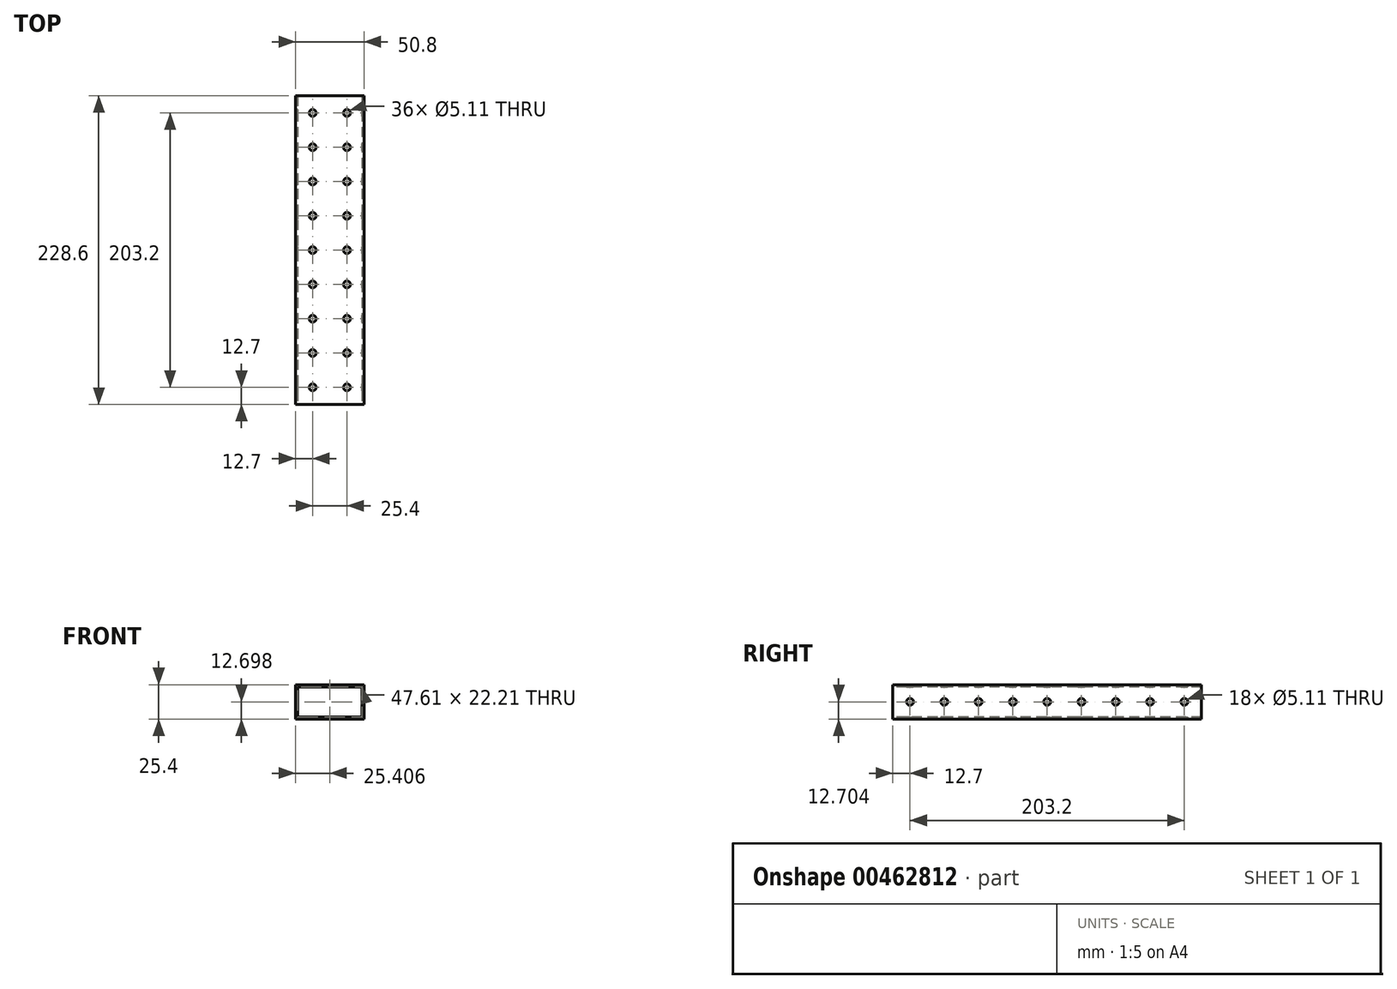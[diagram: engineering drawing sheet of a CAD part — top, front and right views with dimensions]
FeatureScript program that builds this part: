
annotation { "Feature Type Name" : "Feature", "Feature Type Description" : "" }
export const myFeature = defineFeature(function(context is Context, id is Id, definition is map)
    precondition{}
    {
        {
            var Q0;
            Q0=qCreatedBy(makeId("Front.planeOp"),FACE);
            var sketch = newSketch(context, id + "F0", { "sketchPlane" : qUnion([Q0])});
            skLineSegment(sketch, "E0.bottom", {"start": v(-25.4, -41.59) * mm, "end": v(25.4, -41.59) * mm});
            skLineSegment(sketch, "E0.top", {"start": v(-25.4, -66.99) * mm, "end": v(25.4, -66.99) * mm});
            skLineSegment(sketch, "E0.left", {"start": v(-25.4, -41.59) * mm, "end": v(-25.4, -66.99) * mm});
            skLineSegment(sketch, "E0.right", {"start": v(25.4, -41.59) * mm, "end": v(25.4, -66.99) * mm});
            skSolve(sketch);
        }
        {
            var Q0;
            Q0=makeQuery(id+"F0.imprint","IMPRINT",FACE,{"disambiguationData":[TD([[makeQuery(id+"F0.imprint","IMPRINT",EDGE,{"derivedFrom":sQuery(id+"F0.wireOp",EDGE,"E0.bottom")}),-1.0]])]});
            extrude(context, id + "F1", {"entities" : qUnion([Q0]), "depth" : 228.6 * mm});
        }
        {
            var Q0;
            Q0=makeQuery(id+"F1.opExtrude","SWEPT_FACE",FACE,{"disambiguationData":[OSD([sQuery(id+"F0.wireOp",EDGE,"E0.top")])]});
            var sketch = newSketch(context, id + "F2", { "sketchPlane" : qUnion([Q0])});
            skCircle(sketch, "E1", {"center": v(-12.7, 215.9) * mm, "radius": 2.55 * mm});
            skCircle(sketch, "E2.0.1.0", {"center": v(-12.7, 190.5) * mm, "radius": 2.55 * mm});
            skCircle(sketch, "E2.0.2.0", {"center": v(-12.7, 165.1) * mm, "radius": 2.55 * mm});
            skCircle(sketch, "E2.0.3.0", {"center": v(-12.7, 139.7) * mm, "radius": 2.55 * mm});
            skCircle(sketch, "E2.0.4.0", {"center": v(-12.7, 114.3) * mm, "radius": 2.55 * mm});
            skCircle(sketch, "E2.0.5.0", {"center": v(-12.7, 88.9) * mm, "radius": 2.55 * mm});
            skCircle(sketch, "E2.1.0.0", {"center": v(12.7, 215.9) * mm, "radius": 2.55 * mm});
            skCircle(sketch, "E2.1.1.0", {"center": v(12.7, 190.5) * mm, "radius": 2.55 * mm});
            skCircle(sketch, "E2.1.2.0", {"center": v(12.7, 165.1) * mm, "radius": 2.55 * mm});
            skCircle(sketch, "E2.1.3.0", {"center": v(12.7, 139.7) * mm, "radius": 2.55 * mm});
            skCircle(sketch, "E2.1.4.0", {"center": v(12.7, 114.3) * mm, "radius": 2.55 * mm});
            skCircle(sketch, "E2.1.5.0", {"center": v(12.7, 88.9) * mm, "radius": 2.55 * mm});
            skLineSegment(sketch, "E2.direction1", {"start": v(-12.7, 215.9) * mm, "end": v(12.7, 215.9) * mm, "construction": true});
            skLineSegment(sketch, "E2.direction2", {"start": v(-12.7, 215.9) * mm, "end": v(-12.7, 190.5) * mm, "construction": true});
            skCircle(sketch, "E3.0.0.6", {"center": v(-12.7, 63.5) * mm, "radius": 2.55 * mm});
            skCircle(sketch, "E3.0.1.6", {"center": v(12.7, 63.5) * mm, "radius": 2.55 * mm});
            skCircle(sketch, "E4.0.0.7", {"center": v(-12.7, 38.1) * mm, "radius": 2.55 * mm});
            skCircle(sketch, "E4.0.1.7", {"center": v(12.7, 38.1) * mm, "radius": 2.55 * mm});
            skCircle(sketch, "E5.0.0.8", {"center": v(-12.7, 12.7) * mm, "radius": 2.55 * mm});
            skCircle(sketch, "E5.0.1.8", {"center": v(12.7, 12.7) * mm, "radius": 2.55 * mm});
            skSolve(sketch);
        }
        {
            var Q0;
            Q0 = qSketchRegion(id + "F2", true);
            extrude(context, id + "F3", {"entities" : qUnion([Q0]), "operationType" : NewBodyOperationType.REMOVE, "oppositeDirection" : true, "depth" : 76.2 * mm});
        }
        {
            var Q0;
            Q0=makeQuery(id+"F1.opExtrude","CAP_FACE",FACE,{"disambiguationData":[OSD([sQuery(id+"F0.wireOp",EDGE,"E0.bottom"),sQuery(id+"F0.wireOp",EDGE,"E0.top"),sQuery(id+"F0.wireOp",EDGE,"E0.left"),sQuery(id+"F0.wireOp",EDGE,"E0.right")])],"isStart":false});
            var sketch = newSketch(context, id + "F4", { "sketchPlane" : qUnion([Q0])});
            skLineSegment(sketch, "E6.bottom", {"start": v(23.81, -43.19) * mm, "end": v(-23.8, -43.19) * mm});
            skLineSegment(sketch, "E6.top", {"start": v(23.81, -65.4) * mm, "end": v(-23.8, -65.4) * mm});
            skLineSegment(sketch, "E6.left", {"start": v(23.81, -43.19) * mm, "end": v(23.81, -65.4) * mm});
            skLineSegment(sketch, "E6.right", {"start": v(-23.8, -43.19) * mm, "end": v(-23.8, -65.4) * mm});
            skSolve(sketch);
        }
        {
            var Q0;
            Q0 = qSketchRegion(id + "F4", true);
            extrude(context, id + "F5", {"entities" : qUnion([Q0]), "operationType" : NewBodyOperationType.REMOVE, "oppositeDirection" : true, "depth" : 508 * mm});
        }
        {
            var Q0;
            Q0=makeQuery(id+"F1.opExtrude","SWEPT_FACE",FACE,{"disambiguationData":[OSD([sQuery(id+"F0.wireOp",EDGE,"E0.left")])]});
            var sketch = newSketch(context, id + "F6", { "sketchPlane" : qUnion([Q0])});
            skCircle(sketch, "E7", {"center": v(215.9, -54.29) * mm, "radius": 2.55 * mm});
            skCircle(sketch, "E8.1.0.0", {"center": v(190.5, -54.29) * mm, "radius": 2.55 * mm});
            skCircle(sketch, "E8.2.0.0", {"center": v(165.1, -54.29) * mm, "radius": 2.55 * mm});
            skCircle(sketch, "E8.3.0.0", {"center": v(139.7, -54.29) * mm, "radius": 2.55 * mm});
            skCircle(sketch, "E8.4.0.0", {"center": v(114.3, -54.29) * mm, "radius": 2.55 * mm});
            skCircle(sketch, "E8.5.0.0", {"center": v(88.9, -54.29) * mm, "radius": 2.55 * mm});
            skCircle(sketch, "E8.6.0.0", {"center": v(63.5, -54.29) * mm, "radius": 2.55 * mm});
            skCircle(sketch, "E8.7.0.0", {"center": v(38.1, -54.29) * mm, "radius": 2.55 * mm});
            skLineSegment(sketch, "E8.direction1", {"start": v(215.9, -54.29) * mm, "end": v(190.5, -54.29) * mm, "construction": true});
            skCircle(sketch, "E9.0.8.0", {"center": v(12.7, -54.29) * mm, "radius": 2.55 * mm});
            skSolve(sketch);
        }
        {
            var Q0;
            Q0 = qSketchRegion(id + "F6", true);
            extrude(context, id + "F7", {"entities" : qUnion([Q0]), "operationType" : NewBodyOperationType.REMOVE, "oppositeDirection" : true, "depth" : 508 * mm});
        }
    });
